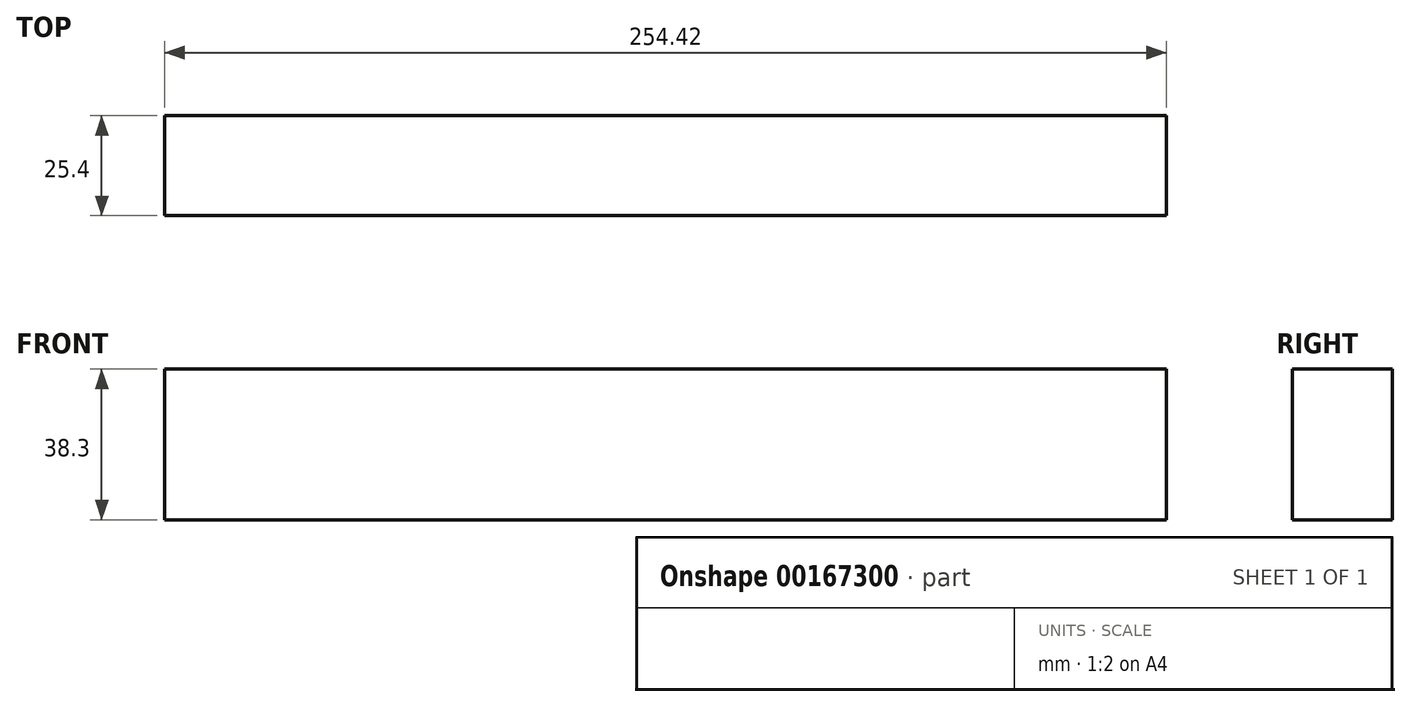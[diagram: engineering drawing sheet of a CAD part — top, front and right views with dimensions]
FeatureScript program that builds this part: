
annotation { "Feature Type Name" : "Feature", "Feature Type Description" : "" }
export const myFeature = defineFeature(function(context is Context, id is Id, definition is map)
    precondition{}
    {
        {
            var Q0;
            Q0=qCreatedBy(makeId("Front.planeOp"),FACE);
            var sketch = newSketch(context, id + "F0", { "sketchPlane" : qUnion([Q0])});
            skLineSegment(sketch, "E0.bottom", {"start": v(-129.86, 30.53) * mm, "end": v(124.56, 30.53) * mm});
            skLineSegment(sketch, "E0.top", {"start": v(-129.86, -7.77) * mm, "end": v(124.56, -7.77) * mm});
            skLineSegment(sketch, "E0.left", {"start": v(-129.86, 30.53) * mm, "end": v(-129.86, -7.77) * mm});
            skLineSegment(sketch, "E0.right", {"start": v(124.56, 30.53) * mm, "end": v(124.56, -7.77) * mm});
            skSolve(sketch);
        }
        {
            var Q0;
            Q0=qSketchRegion(id+"F0",true);
            extrude(context, id + "F1", {"entities" : qUnion([Q0]), "depth" : 25.4 * mm});
        }
    });
